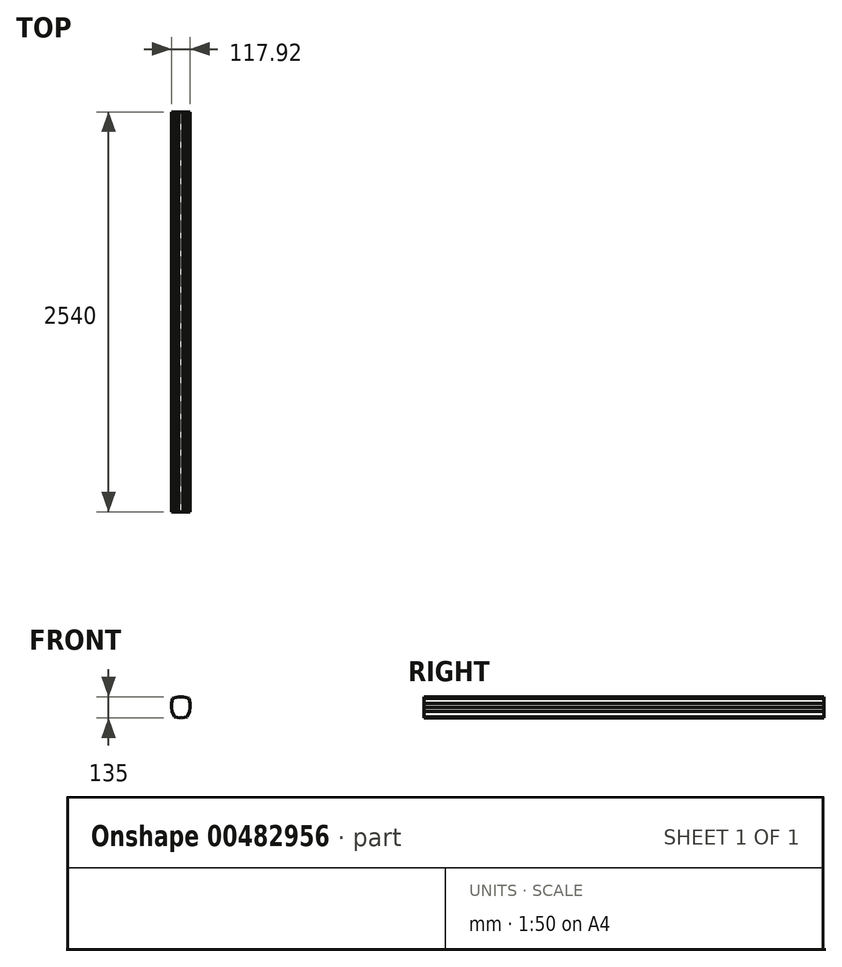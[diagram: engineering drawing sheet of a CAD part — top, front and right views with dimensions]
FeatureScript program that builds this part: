
annotation { "Feature Type Name" : "Feature", "Feature Type Description" : "" }
export const myFeature = defineFeature(function(context is Context, id is Id, definition is map)
    precondition{}
    {
        {
            var Q0;
            Q0=qCreatedBy(makeId("Front.planeOp"),FACE);
            var sketch = newSketch(context, id + "F0", { "sketchPlane" : qUnion([Q0])});
            skLineSegment(sketch, "E0", {"start": v(-7.02, -52.9) * mm, "end": v(-22, -47.97) * mm});
            skLineSegment(sketch, "E1", {"start": v(-22, -47.97) * mm, "end": v(-37.16, -21.3) * mm});
            skLineSegment(sketch, "E2", {"start": v(-37.16, -21.3) * mm, "end": v(-37.84, -13.18) * mm});
            skLineSegment(sketch, "E3", {"start": v(-37.84, -13.18) * mm, "end": v(-22.73, -31.22) * mm});
            skLineSegment(sketch, "E4", {"start": v(-22.73, -31.22) * mm, "end": v(-11.57, -39.25) * mm});
            skLineSegment(sketch, "E5", {"start": v(-11.57, -39.25) * mm, "end": v(-6.83, -39.25) * mm});
            skLineSegment(sketch, "E6", {"start": v(-6.83, -39.25) * mm, "end": v(0, -40.76) * mm});
            skLineSegment(sketch, "E7.MirrorCS", {"start": v(6.83, -39.25) * mm, "end": v(0, -40.76) * mm});
            skLineSegment(sketch, "E8.MirrorCS", {"start": v(11.57, -39.25) * mm, "end": v(6.83, -39.25) * mm});
            skLineSegment(sketch, "E9.MirrorCS", {"start": v(22.73, -31.22) * mm, "end": v(11.57, -39.25) * mm});
            skLineSegment(sketch, "E10.MirrorCS", {"start": v(37.84, -13.18) * mm, "end": v(22.73, -31.22) * mm});
            skLineSegment(sketch, "E11.MirrorCS", {"start": v(37.16, -21.3) * mm, "end": v(37.84, -13.18) * mm});
            skLineSegment(sketch, "E12.MirrorCS", {"start": v(22, -47.97) * mm, "end": v(37.16, -21.3) * mm});
            skLineSegment(sketch, "E13.MirrorCS", {"start": v(7.02, -52.9) * mm, "end": v(22, -47.97) * mm});
            skLineSegment(sketch, "E14", {"start": v(0, -67.3) * mm, "end": v(-5.3, -71.67) * mm});
            skLineSegment(sketch, "E15", {"start": v(-5.3, -71.67) * mm, "end": v(-39.84, -63.04) * mm});
            skLineSegment(sketch, "E16", {"start": v(-39.84, -63.04) * mm, "end": v(-56.12, -30.71) * mm});
            skLineSegment(sketch, "E17", {"start": v(-56.12, -30.53) * mm, "end": v(-58.59, -3.22) * mm});
            skLineSegment(sketch, "E18", {"start": v(-58.59, -3.22) * mm, "end": v(-58.96, 22.75) * mm});
            skLineSegment(sketch, "E19", {"start": v(-58.96, 22.75) * mm, "end": v(-58.96, 22.75) * mm});
            skLineSegment(sketch, "E20", {"start": v(-58.96, 22.75) * mm, "end": v(-53.84, 52.32) * mm});
            skLineSegment(sketch, "E21", {"start": v(-53.84, 52.32) * mm, "end": v(-31.28, 60.86) * mm});
            skLineSegment(sketch, "E22", {"start": v(-31.28, 60.86) * mm, "end": v(-13.65, 63.33) * mm});
            skLineSegment(sketch, "E23", {"start": v(-13.65, 63.33) * mm, "end": v(0, 63.33) * mm});
            skLineSegment(sketch, "E24.MirrorCS", {"start": v(13.65, 63.33) * mm, "end": v(0, 63.33) * mm});
            skLineSegment(sketch, "E25.MirrorCS", {"start": v(31.28, 60.86) * mm, "end": v(13.65, 63.33) * mm});
            skLineSegment(sketch, "E26.MirrorCS", {"start": v(53.84, 52.32) * mm, "end": v(31.28, 60.86) * mm});
            skLineSegment(sketch, "E27.MirrorCS", {"start": v(58.96, 22.75) * mm, "end": v(53.84, 52.32) * mm});
            skLineSegment(sketch, "E28.MirrorCS", {"start": v(58.96, 22.75) * mm, "end": v(58.96, 22.75) * mm});
            skLineSegment(sketch, "E29.MirrorCS", {"start": v(58.59, -3.22) * mm, "end": v(58.96, 22.75) * mm});
            skLineSegment(sketch, "E30.MirrorCS", {"start": v(56.12, -30.53) * mm, "end": v(58.59, -3.22) * mm});
            skLineSegment(sketch, "E31.MirrorCS", {"start": v(39.84, -63.04) * mm, "end": v(56.12, -30.71) * mm});
            skLineSegment(sketch, "E32.MirrorCS", {"start": v(5.3, -71.67) * mm, "end": v(39.84, -63.04) * mm});
            skLineSegment(sketch, "E33.MirrorCS", {"start": v(0, -67.3) * mm, "end": v(5.3, -71.67) * mm});
            skFitSpline(sketch, "E34", {"points": [v(-37.05, 16.22) * mm, v(-17.73, 21.28) * mm, v(-13.29, 11.91) * mm, v(-24.72, 8.1) * mm, v(-37.05, 16.22) * mm]});
            skFitSpline(sketch, "E35.MirrorC", {"points": [v(37.05, 16.22) * mm, v(17.73, 21.28) * mm, v(13.29, 11.91) * mm, v(24.72, 8.1) * mm, v(37.05, 16.22) * mm]});
            skLineSegment(sketch, "E36", {"start": v(3.35, 28.8) * mm, "end": v(12.06, 30.77) * mm});
            skLineSegment(sketch, "E37", {"start": v(12.06, 30.77) * mm, "end": v(20.36, 30.46) * mm});
            skLineSegment(sketch, "E38", {"start": v(20.36, 30.46) * mm, "end": v(29.07, 29.3) * mm});
            skLineSegment(sketch, "E39", {"start": v(29.07, 29.3) * mm, "end": v(40.97, 27.1) * mm});
            skLineSegment(sketch, "E40", {"start": v(40.97, 27.1) * mm, "end": v(50.1, 25.93) * mm});
            skLineSegment(sketch, "E41", {"start": v(50.1, 25.93) * mm, "end": v(28.18, 31.19) * mm});
            skLineSegment(sketch, "E42", {"start": v(28.18, 31.19) * mm, "end": v(15.49, 32.16) * mm});
            skLineSegment(sketch, "E43", {"start": v(15.49, 32.16) * mm, "end": v(6.27, 30.17) * mm});
            skLineSegment(sketch, "E44", {"start": v(6.27, 30.17) * mm, "end": v(3.35, 28.8) * mm});
            skLineSegment(sketch, "E45.0", {"start": v(28.18, 31.19) * mm, "end": v(29.07, 29.3) * mm, "construction": true});
            skLineSegment(sketch, "E46.MirrorCS", {"start": v(-40.97, 27.1) * mm, "end": v(-50.1, 25.93) * mm});
            skLineSegment(sketch, "E47.MirrorCS", {"start": v(-29.07, 29.3) * mm, "end": v(-40.97, 27.1) * mm});
            skLineSegment(sketch, "E48.MirrorCS", {"start": v(-50.1, 25.93) * mm, "end": v(-28.18, 31.19) * mm});
            skLineSegment(sketch, "E49.MirrorCS", {"start": v(-12.06, 30.77) * mm, "end": v(-20.36, 30.46) * mm});
            skLineSegment(sketch, "E50.MirrorCS", {"start": v(-28.18, 31.19) * mm, "end": v(-15.49, 32.16) * mm});
            skLineSegment(sketch, "E51.MirrorCS", {"start": v(-20.36, 30.46) * mm, "end": v(-29.07, 29.3) * mm});
            skLineSegment(sketch, "E52.MirrorCS", {"start": v(-3.35, 28.8) * mm, "end": v(-12.06, 30.77) * mm});
            skLineSegment(sketch, "E53.MirrorCS", {"start": v(-6.27, 30.17) * mm, "end": v(-3.35, 28.8) * mm});
            skLineSegment(sketch, "E54.MirrorCS", {"start": v(-15.49, 32.16) * mm, "end": v(-6.27, 30.17) * mm});
            skLineSegment(sketch, "E55", {"start": v(-36.63, 14.04) * mm, "end": v(-29.37, 16.22) * mm});
            skLineSegment(sketch, "E56", {"start": v(-29.37, 16.22) * mm, "end": v(-23.3, 17.26) * mm});
            skLineSegment(sketch, "E57", {"start": v(-23.3, 17.26) * mm, "end": v(-16.95, 16.22) * mm});
            skLineSegment(sketch, "E58", {"start": v(-16.95, 16.22) * mm, "end": v(-12.8, 14.32) * mm});
            skLineSegment(sketch, "E59.MirrorCS", {"start": v(16.95, 16.22) * mm, "end": v(12.8, 14.32) * mm});
            skLineSegment(sketch, "E60.MirrorCS", {"start": v(23.3, 17.26) * mm, "end": v(16.95, 16.22) * mm});
            skLineSegment(sketch, "E61.MirrorCS", {"start": v(29.37, 16.22) * mm, "end": v(23.3, 17.26) * mm});
            skLineSegment(sketch, "E62.MirrorCS", {"start": v(36.63, 14.04) * mm, "end": v(29.37, 16.22) * mm});
            skCircle(sketch, "E63", {"center": v(-23.2, 12.61) * mm, "radius": 3.73 * mm});
            skCircle(sketch, "E64.MirrorC", {"center": v(23.2, 12.61) * mm, "radius": 3.73 * mm});
            skLineSegment(sketch, "E65", {"start": v(-2.72, -19.34) * mm, "end": v(-5.3, -18.33) * mm});
            skLineSegment(sketch, "E66", {"start": v(-5.3, -18.33) * mm, "end": v(-6.66, -16.86) * mm});
            skLineSegment(sketch, "E67", {"start": v(-6.66, -16.86) * mm, "end": v(-5.76, -14.15) * mm});
            skLineSegment(sketch, "E68", {"start": v(-5.76, -14.15) * mm, "end": v(-3.28, -5.14) * mm});
            skLineSegment(sketch, "E69", {"start": v(-3.28, -5.14) * mm, "end": v(-0.01, -1.3) * mm});
            skLineSegment(sketch, "E70", {"start": v(-2.72, -19.34) * mm, "end": v(-0.01, -20.24) * mm});
            skLineSegment(sketch, "E71.MirrorCS", {"start": v(3.28, -5.14) * mm, "end": v(0.01, -1.3) * mm});
            skLineSegment(sketch, "E72.MirrorCS", {"start": v(5.76, -14.15) * mm, "end": v(3.28, -5.14) * mm});
            skLineSegment(sketch, "E73.MirrorCS", {"start": v(6.66, -16.86) * mm, "end": v(5.76, -14.15) * mm});
            skLineSegment(sketch, "E74.MirrorCS", {"start": v(5.3, -18.33) * mm, "end": v(6.66, -16.86) * mm});
            skLineSegment(sketch, "E75.MirrorCS", {"start": v(2.72, -19.34) * mm, "end": v(5.3, -18.33) * mm});
            skLineSegment(sketch, "E76.MirrorCS", {"start": v(2.72, -19.34) * mm, "end": v(0.01, -20.24) * mm});
            skLineSegment(sketch, "E77", {"start": v(-7.02, -52.9) * mm, "end": v(0, -54.29) * mm});
            skLineSegment(sketch, "E78", {"start": v(0, -54.29) * mm, "end": v(7.02, -52.9) * mm});
            skSolve(sketch);
        }
        {
            var Q0;
            Q0=sQuery(id+"F0.wireOp",EDGE,"E21");
            var Q1;
            Q1=sQuery(id+"F0.wireOp",EDGE,"E20");
            var Q2;
            Q2=sQuery(id+"F0.wireOp",EDGE,"E18");
            var Q3;
            Q3=sQuery(id+"F0.wireOp",EDGE,"E17");
            var Q4;
            Q4=sQuery(id+"F0.wireOp",EDGE,"E16");
            var Q5;
            Q5=sQuery(id+"F0.wireOp",EDGE,"E15");
            var Q6;
            Q6=sQuery(id+"F0.wireOp",EDGE,"E14");
            var Q7;
            Q7=sQuery(id+"F0.wireOp",EDGE,"E33.MirrorCS");
            var Q8;
            Q8=sQuery(id+"F0.wireOp",EDGE,"E32.MirrorCS");
            var Q9;
            Q9=sQuery(id+"F0.wireOp",EDGE,"E31.MirrorCS");
            var Q10;
            Q10=sQuery(id+"F0.wireOp",EDGE,"E30.MirrorCS");
            var Q11;
            Q11=sQuery(id+"F0.wireOp",EDGE,"E29.MirrorCS");
            var Q12;
            Q12=sQuery(id+"F0.wireOp",EDGE,"E27.MirrorCS");
            var Q13;
            Q13=sQuery(id+"F0.wireOp",EDGE,"E26.MirrorCS");
            var Q14;
            Q14=sQuery(id+"F0.wireOp",EDGE,"E25.MirrorCS");
            var Q15;
            Q15=sQuery(id+"F0.wireOp",EDGE,"E24.MirrorCS");
            var Q16;
            Q16=sQuery(id+"F0.wireOp",EDGE,"E23");
            var Q17;
            Q17=sQuery(id+"F0.wireOp",EDGE,"E22");
            extrude(context, id + "F1", {"bodyType" : ToolBodyType.SURFACE, "surfaceEntities" : qUnion([Q0, Q1, Q2, Q3, Q4, Q5, Q6, Q7, Q8, Q9, Q10, Q11, Q12, Q13, Q14, Q15, Q16, Q17]), "depth" : 2540 * mm});
        }
    });
